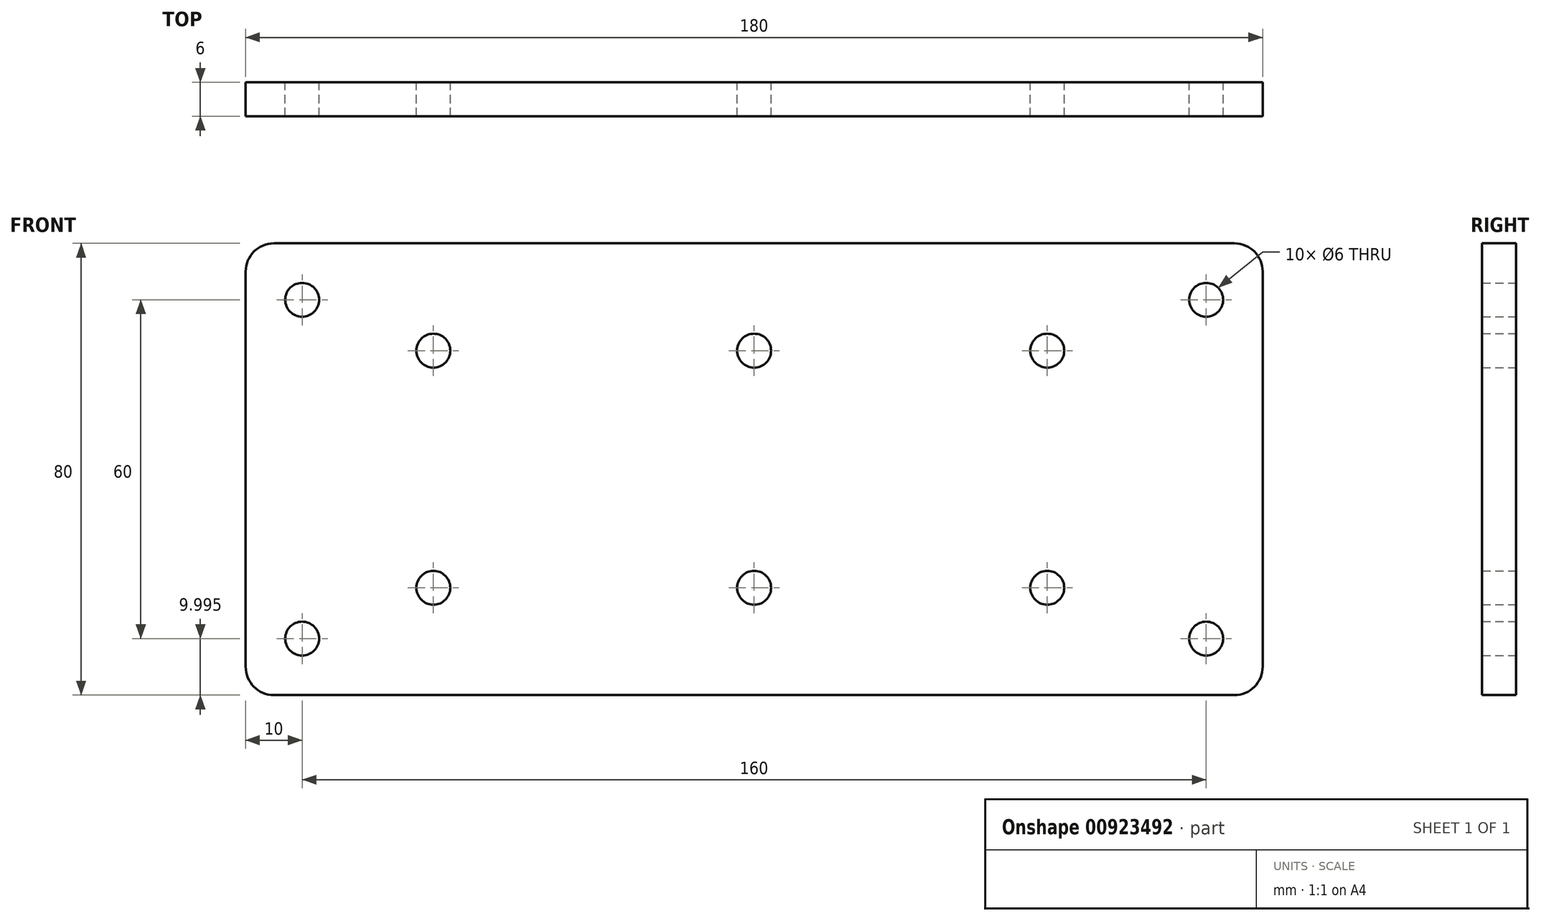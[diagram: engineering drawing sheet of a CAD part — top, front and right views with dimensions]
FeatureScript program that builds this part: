
annotation { "Feature Type Name" : "Feature", "Feature Type Description" : "" }
export const myFeature = defineFeature(function(context is Context, id is Id, definition is map)
    precondition{}
    {
        {
            var Q0;
            Q0=qCreatedBy(makeId("Front.planeOp"),FACE);
            var sketch = newSketch(context, id + "F0", { "sketchPlane" : qUnion([Q0])});
            skLineSegment(sketch, "E0", {"start": v(-90, 44.42) * mm, "end": v(90, 44.42) * mm});
            skLineSegment(sketch, "E1", {"start": v(90, 44.42) * mm, "end": v(90, -35.58) * mm});
            skLineSegment(sketch, "E2", {"start": v(90, -35.58) * mm, "end": v(-90, -35.58) * mm});
            skLineSegment(sketch, "E3", {"start": v(-90, -35.58) * mm, "end": v(-90, 44.42) * mm});
            skLineSegment(sketch, "E4", {"start": v(0, -35.58) * mm, "end": v(0, 44.42) * mm, "construction": true});
            skLineSegment(sketch, "E5", {"start": v(-90, 4.42) * mm, "end": v(90, 4.42) * mm, "construction": true});
            skCircle(sketch, "E6", {"center": v(80, 34.42) * mm, "radius": 3 * mm});
            skCircle(sketch, "E7", {"center": v(-80, 34.42) * mm, "radius": 3 * mm});
            skCircle(sketch, "E8", {"center": v(80, -25.58) * mm, "radius": 3 * mm});
            skCircle(sketch, "E9", {"center": v(-56.78, 25.42) * mm, "radius": 3 * mm});
            skCircle(sketch, "E10", {"center": v(0, 25.42) * mm, "radius": 3 * mm});
            skCircle(sketch, "E11", {"center": v(51.88, 25.42) * mm, "radius": 3 * mm});
            skCircle(sketch, "E12", {"center": v(-56.78, -16.58) * mm, "radius": 3 * mm});
            skCircle(sketch, "E13", {"center": v(0, -16.58) * mm, "radius": 3 * mm});
            skCircle(sketch, "E14", {"center": v(51.88, -16.58) * mm, "radius": 3 * mm});
            skCircle(sketch, "E15", {"center": v(-80, -25.58) * mm, "radius": 3 * mm});
            skSolve(sketch);
        }
        {
            var Q0;
            Q0 = qSketchRegion(id + "F0", true);
            extrude(context, id + "F1", {"entities" : qUnion([Q0]), "depth" : 6 * mm, "offsetDistance" : 25 * mm});
        }
        {
            var Q0;
            Q0=makeQuery(id+"F1.opExtrude","SWEPT_EDGE",EDGE,{"disambiguationData":[OSD([sQuery(id+"F0.wireOp",EDGE,"E0"),sQuery(id+"F0.wireOp",EDGE,"E3")])]});
            var Q1;
            Q1=makeQuery(id+"F1.opExtrude","SWEPT_EDGE",EDGE,{"disambiguationData":[OSD([sQuery(id+"F0.wireOp",EDGE,"E2"),sQuery(id+"F0.wireOp",EDGE,"E3")])]});
            var Q2;
            Q2=makeQuery(id+"F1.opExtrude","SWEPT_EDGE",EDGE,{"disambiguationData":[OSD([sQuery(id+"F0.wireOp",EDGE,"E0"),sQuery(id+"F0.wireOp",EDGE,"E1")])]});
            var Q3;
            Q3=makeQuery(id+"F1.opExtrude","SWEPT_EDGE",EDGE,{"disambiguationData":[OSD([sQuery(id+"F0.wireOp",EDGE,"E1"),sQuery(id+"F0.wireOp",EDGE,"E2")])]});
            fillet(context, id + "F2", {"entities" : qUnion([Q0, Q1, Q2, Q3]), "radius" : 5 * mm, "tangentPropagation" : true, "allowEdgeOverflow" : false});
        }
    });
